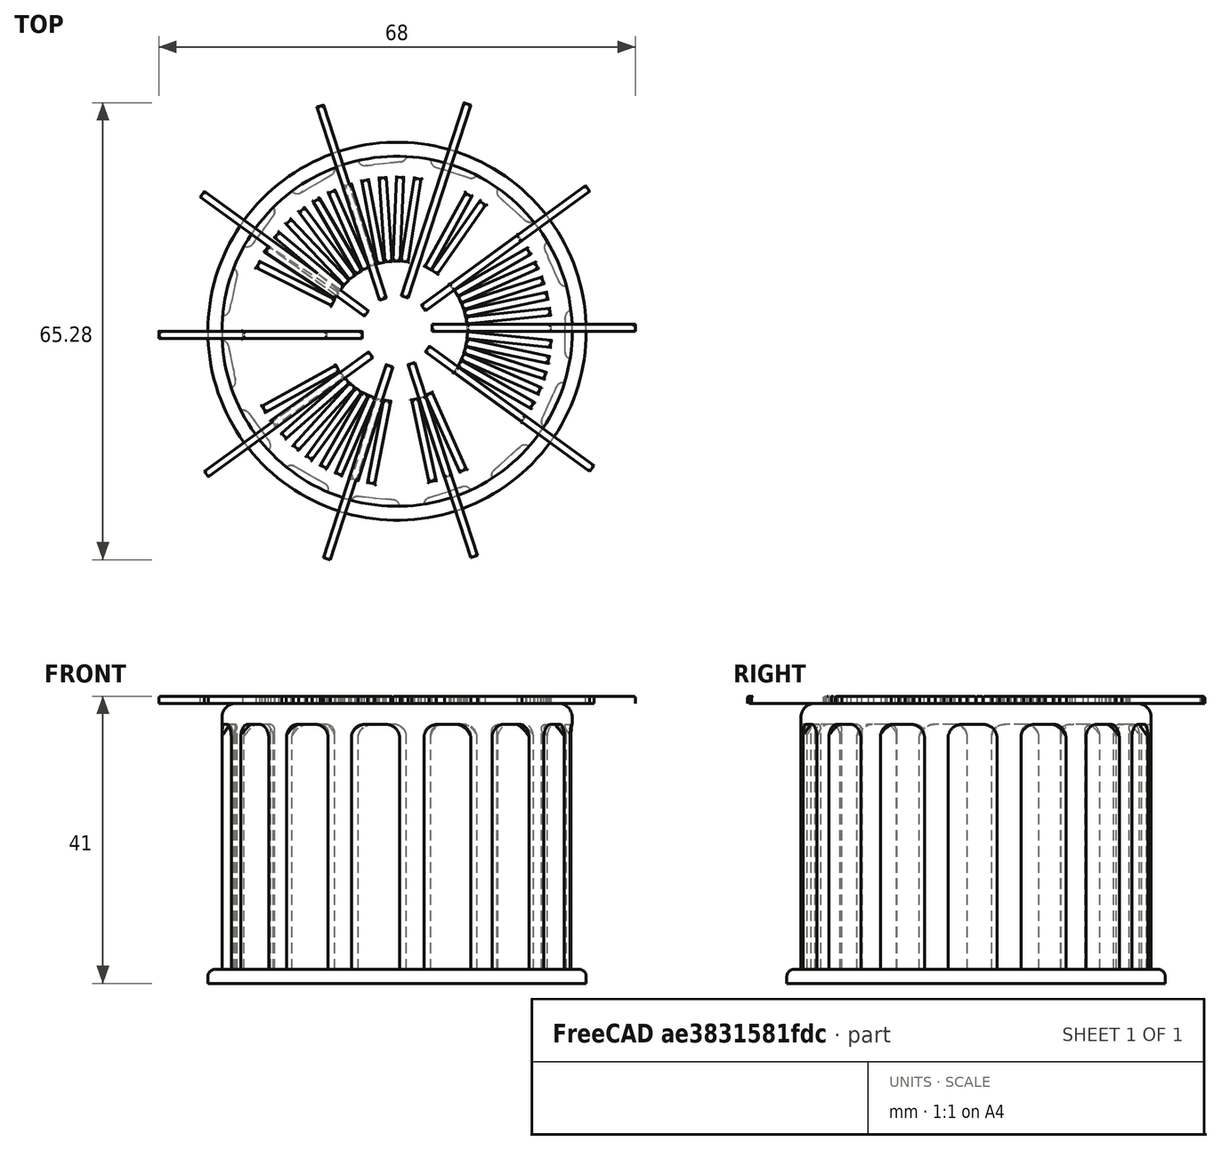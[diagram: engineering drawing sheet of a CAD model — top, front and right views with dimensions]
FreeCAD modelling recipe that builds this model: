
FCSTD DOCUMENT  (FreeCAD 0.18R14220 (Git))
Label: bolardo
License: All rights reserved
LicenseURL: http://en.wikipedia.org/wiki/All_rights_reserved
objects: Part::Fillet×11, Part::Box×8, Part::FeaturePython×7, Part::MultiFuse×7, Part::Cylinder×2, Part::Cut×1
note: 36 computed .brp shape members not serialized (recipe doc carries the construction recipe); baked Part::Feature solids carry a one-line shape summary decoded from their .brp

FEATURE [Part::Cylinder] Cylinder  label="Cilindro"
  Angle = 360
  AttacherType = Attacher::AttachEngine3D
  Height = 40
  Radius = 25
FEATURE [Part::Box] Box  label="Cubo"
  AttacherType = Attacher::AttachEngine3D
  Height = 37
  Length = 4
  Width = 7
FEATURE [Part::Fillet] Fillet
  Base = -> Box
  Edges = 6 edges: [Edge1 r=1,Edge3 r=1,Edge5 r=1,Edge7 r=1,Edge10 r=2,Edge12 r=2]
FEATURE [Part::FeaturePython] Array001  # Draft array (typed FeaturePython)
  Angle = 360
  ArrayType = 1
  Axis = (0,0,1)
  Base = -> Fillet
  Center = (-24,4,0)
  Fuse = false
  IntervalAxis = (0,0,0)
  IntervalX = (1,0,0)
  IntervalY = (0,1,0)
  IntervalZ = (0,0,1)
  NumberPolar = 15
  NumberX = 2
  NumberY = 2
  NumberZ = 1
  Placement = pos=(24,-4,0) rot=(0,0,1;0rad)
FEATURE [Part::Cut] Cut
  Base = -> Cylinder
  Refine = true
  Tool = -> Array001
FEATURE [Part::Fillet] Fillet001  label="bolardo solo"
  Base = -> Cut
  Edges = 1 edges r=2: [Edge93]
FEATURE [Part::Box] Box001  label="Cubo001"
  AttacherType = Attacher::AttachEngine3D
  Height = 1
  Length = 12
  Placement = pos=(0,0,40) rot=(0,0,1;0rad)
  Width = 1
FEATURE [Part::Fillet] Fillet002
  Base = -> Box001
  Edges = 4 edges r=0.25: [Edge2,Edge6,Edge10,Edge12]
FEATURE [Part::FeaturePython] Array002  label="13"  # Draft array (typed FeaturePython)
  Angle = 72
  ArrayType = 1
  Axis = (0,0,1)
  Base = -> Fillet002
  Center = (-10,0,0)
  Fuse = false
  IntervalAxis = (0,0,0)
  IntervalX = (1,0,0)
  IntervalY = (0,1,0)
  IntervalZ = (0,0,1)
  NumberPolar = 13
  NumberX = 2
  NumberY = 2
  NumberZ = 1
  Placement = pos=(8.09017,-5.87785,0) rot=(0,0,-1;0.628319rad)
FEATURE [Part::Box] Box002  label="Cubo002"
  AttacherType = Attacher::AttachEngine3D
  Height = 1
  Length = 29
  Placement = pos=(0,0,40) rot=(0,0,1;0rad)
  Width = 1
FEATURE [Part::Fillet] Fillet003
  Base = -> Box002
  Edges = 4 edges r=0.25: [Edge2,Edge6,Edge10,Edge12]
FEATURE [Part::FeaturePython] Array003  label="guia"  # Draft array (typed FeaturePython)
  Angle = 360
  ArrayType = 1
  Axis = (0,0,1)
  Base = -> Fillet003
  Center = (-5,0,0)
  Fuse = false
  IntervalAxis = (0,0,0)
  IntervalX = (1,0,0)
  IntervalY = (0,1,0)
  IntervalZ = (0,0,1)
  NumberPolar = 10
  NumberX = 2
  NumberY = 2
  NumberZ = 1
  Placement = pos=(5,0,0) rot=(0,0,1;0rad)
FEATURE [Part::Box] Box003  label="Cubo003"
  AttacherType = Attacher::AttachEngine3D
  Height = 1
  Length = 12
  Placement = pos=(0,0,40) rot=(0,0,1;0rad)
  Width = 1
FEATURE [Part::Fillet] Fillet004
  Base = -> Box003
  Edges = 4 edges r=0.25: [Edge2,Edge6,Edge10,Edge12]
FEATURE [Part::FeaturePython] Array004  label="12"  # Draft array (typed FeaturePython)
  Angle = 72
  ArrayType = 1
  Axis = (0,0,1)
  Base = -> Fillet004
  Center = (-10,0,0)
  Fuse = false
  IntervalAxis = (0,0,0)
  IntervalX = (1,0,0)
  IntervalY = (0,1,0)
  IntervalZ = (0,0,1)
  NumberPolar = 12
  NumberX = 2
  NumberY = 2
  NumberZ = 1
  Placement = pos=(1.56434,9.87688,0) rot=(0,0,1;1.41372rad)
FEATURE [Part::Box] Box004  label="Cubo004"
  AttacherType = Attacher::AttachEngine3D
  Height = 1
  Length = 12
  Placement = pos=(0,0,40) rot=(0,0,1;0rad)
  Width = 1
FEATURE [Part::Fillet] Fillet005
  Base = -> Box004
  Edges = 4 edges r=0.25: [Edge2,Edge6,Edge10,Edge12]
FEATURE [Part::FeaturePython] Array005  label="2"  # Draft array (typed FeaturePython)
  Angle = 6
  ArrayType = 1
  Axis = (0,0,1)
  Base = -> Fillet005
  Center = (-10,0,0)
  Fuse = false
  IntervalAxis = (0,0,0)
  IntervalX = (0,0,0)
  IntervalY = (0,0,0)
  IntervalZ = (0,0,0)
  NumberPolar = 2
  NumberX = 2
  NumberY = 2
  NumberZ = 1
  Placement = pos=(5.73576,8.19152,0) rot=(0,0,1;0.959931rad)
FEATURE [Part::Box] Box005  label="Cubo005"
  AttacherType = Attacher::AttachEngine3D
  Height = 1
  Length = 12
  Placement = pos=(0,0,40) rot=(0,0,1;0rad)
  Width = 1
FEATURE [Part::Fillet] Fillet006
  Base = -> Box005
  Edges = 4 edges r=0.25: [Edge2,Edge6,Edge10,Edge12]
FEATURE [Part::FeaturePython] Array006  label="3"  # Draft array (typed FeaturePython)
  Angle = 12
  ArrayType = 1
  Axis = (0,0,1)
  Base = -> Fillet006
  Center = (-10,0,0)
  Fuse = false
  IntervalAxis = (0,0,0)
  IntervalX = (0,0,0)
  IntervalY = (0,0,0)
  IntervalZ = (0,0,0)
  NumberPolar = 3
  NumberX = 2
  NumberY = 2
  NumberZ = 1
  Placement = pos=(2.07912,-9.78148,0) rot=(0,0,-1;1.36136rad)
FEATURE [Part::Box] Box006  label="Cubo006"
  AttacherType = Attacher::AttachEngine3D
  Height = 1
  Length = 12
  Placement = pos=(0,0,40) rot=(0,0,1;0rad)
  Width = 1
FEATURE [Part::Fillet] Fillet007
  Base = -> Box006
  Edges = 4 edges r=0.25: [Edge2,Edge6,Edge10,Edge12]
FEATURE [Part::FeaturePython] Array007  label="9"  # Draft array (typed FeaturePython)
  Angle = 50
  ArrayType = 1
  Axis = (0,0,1)
  Base = -> Fillet007
  Center = (-10,0,0)
  Fuse = false
  IntervalAxis = (0,0,0)
  IntervalX = (0,0,0)
  IntervalY = (0,0,0)
  IntervalZ = (0,0,0)
  NumberPolar = 9
  NumberX = 2
  NumberY = 2
  NumberZ = 1
  Placement = pos=(-8.7462,-4.8481,0) rot=(0,0,1;3.64774rad)
FEATURE [Part::Box] Box007  label="Cubo007"
  AttacherType = Attacher::AttachEngine3D
  Height = 1
  Length = 12
  Placement = pos=(0,0,40) rot=(0,0,1;0rad)
  Width = 1
FEATURE [Part::Fillet] Fillet008  label="1"
  Base = -> Box007
  Edges = 4 edges r=0.25: [Edge2,Edge6,Edge10,Edge12]
  Placement = pos=(-22,-1,0) rot=(0,0,1;0rad)
FEATURE [Part::Cylinder] Cylinder001  label="Cilindro001"
  Angle = 360
  AttacherType = Attacher::AttachEngine3D
  Height = 2
  Radius = 27
FEATURE [Part::Fillet] Fillet009  label="base"
  Base = -> Cylinder001
  Edges = 1 edges r=1: [Edge1]
FEATURE [Part::MultiFuse] Fusion  label="bolardo con base"
  Refine = true
  Shapes = -> [Fillet009,Fillet001]
FEATURE [Part::MultiFuse] Fusion002
  Refine = true
  Shapes = -> [Array002,Array004]
FEATURE [Part::MultiFuse] Fusion003
  Refine = true
  Shapes = -> [Fusion002,Array005]
FEATURE [Part::MultiFuse] Fusion004
  Refine = true
  Shapes = -> [Fusion003,Array006]
FEATURE [Part::MultiFuse] Fusion005
  Refine = true
  Shapes = -> [Fusion004,Array007]
FEATURE [Part::MultiFuse] Fusion006  label="lineas superiores"
  Refine = true
  Shapes = -> [Fusion005,Fillet008]
FEATURE [Part::MultiFuse] Fusion007
  Refine = true
  Shapes = -> [Fusion,Fusion006]
FEATURE [Part::Fillet] Fillet010  label="bolardo completo"
  Base = -> Fusion007
  Edges = 52 edges r=0.2: [Edge283,Edge284,Edge287,Edge288,Edge290,Edge291,Edge295,Edge299,Edge303,Edge307,Edge311,Edge315,Edge319,Edge323,Edge326,Edge327,Edge331,Edge334,Edge335,Edge339,Edge343,Edge344,Edge347,Edge351,Edge355,Edge358,Edge359,Edge363,Edge364,Edge367,Edge371,Edge375,Edge379,Edge383,Edge387,Edge391,Edge395,+15 more]
